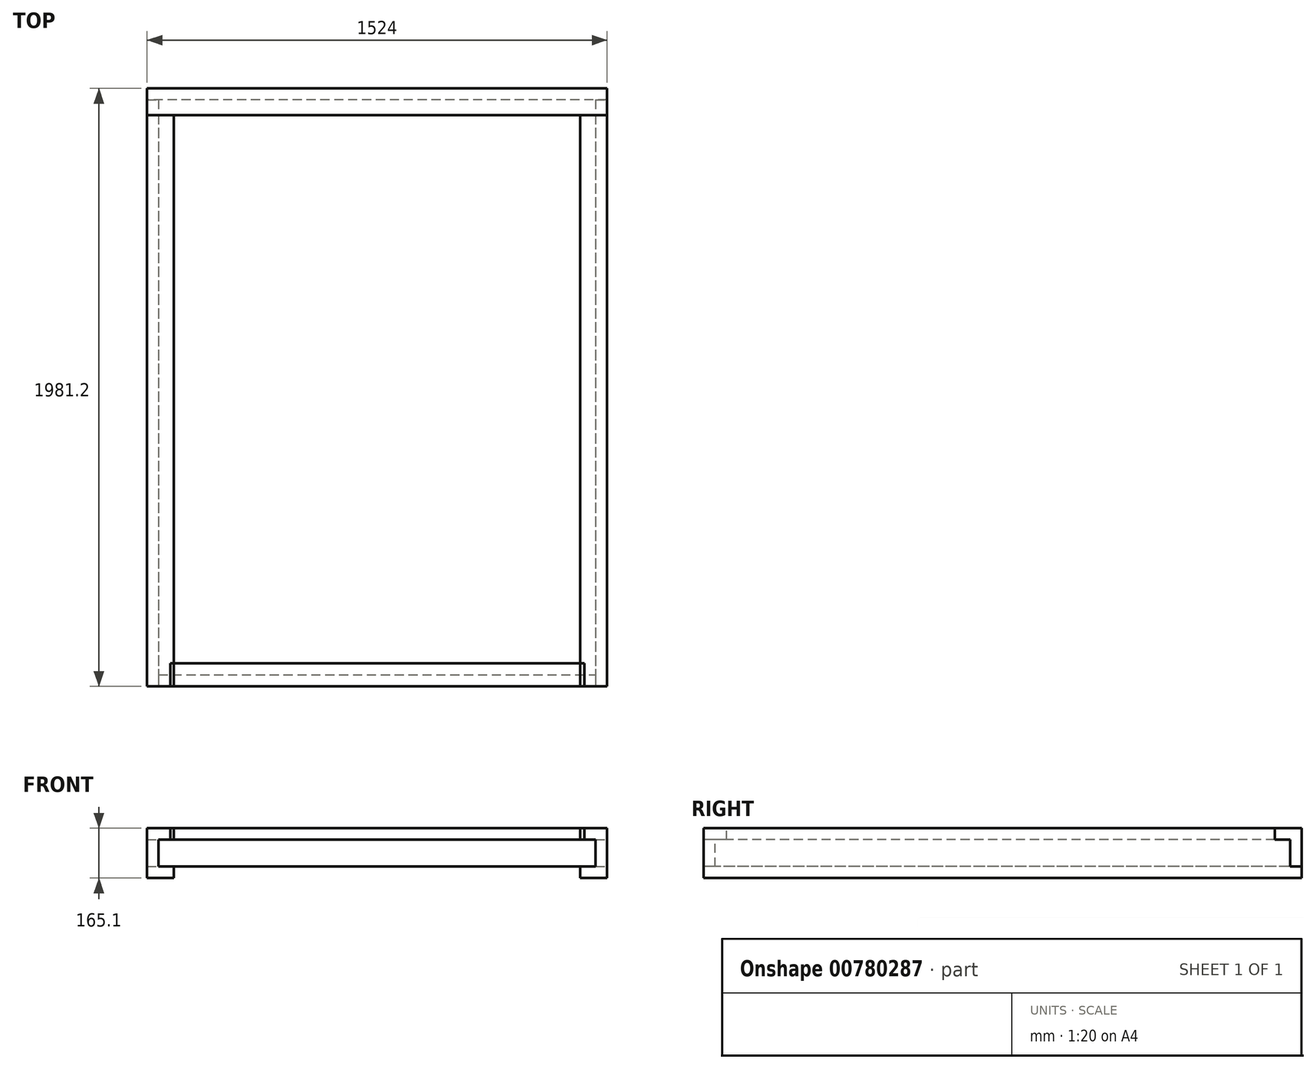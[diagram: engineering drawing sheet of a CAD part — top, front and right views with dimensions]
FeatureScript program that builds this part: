
annotation { "Feature Type Name" : "Feature", "Feature Type Description" : "" }
export const myFeature = defineFeature(function(context is Context, id is Id, definition is map)
    precondition{}
    {
        {
            var Q0;
            Q0=qCreatedBy(makeId("Front.planeOp"),FACE);
            var sketch = newSketch(context, id + "F0", { "sketchPlane" : qUnion([Q0])});
            skLineSegment(sketch, "E0", {"start": v(0, 0) * mm, "end": v(88.9, 0) * mm});
            skLineSegment(sketch, "E1", {"start": v(88.9, 0) * mm, "end": v(88.9, 38.1) * mm});
            skLineSegment(sketch, "E2", {"start": v(88.9, 38.1) * mm, "end": v(0, 38.1) * mm});
            skLineSegment(sketch, "E3", {"start": v(0, 38.1) * mm, "end": v(0, 0) * mm});
            skLineSegment(sketch, "E4.bottom", {"start": v(0, 38.1) * mm, "end": v(38.1, 38.1) * mm});
            skLineSegment(sketch, "E4.top", {"start": v(0, 127) * mm, "end": v(38.1, 127) * mm});
            skLineSegment(sketch, "E4.left", {"start": v(0, 38.1) * mm, "end": v(0, 127) * mm});
            skLineSegment(sketch, "E4.right", {"start": v(38.1, 38.1) * mm, "end": v(38.1, 127) * mm});
            skLineSegment(sketch, "E5.bottom", {"start": v(0, 127) * mm, "end": v(88.9, 127) * mm});
            skLineSegment(sketch, "E5.top", {"start": v(0, 165.1) * mm, "end": v(88.9, 165.1) * mm});
            skLineSegment(sketch, "E5.left", {"start": v(0, 127) * mm, "end": v(0, 165.1) * mm});
            skLineSegment(sketch, "E5.right", {"start": v(88.9, 127) * mm, "end": v(88.9, 165.1) * mm});
            skSolve(sketch);
        }
        {
            var Q0;
            Q0 = qSketchRegion(id + "F0", true);
            extrude(context, id + "F1", {"entities" : qUnion([Q0]), "oppositeDirection" : true, "depth" : 1981.2 * mm, "offsetDistance" : 25.4 * mm});
        }
        {
            var Q0;
            Q0=qCreatedBy(makeId("Right.planeOp"),FACE);
            cPlane(context, id + "F2", {"entities" : qUnion([Q0]), "cplaneType" : CPlaneType.OFFSET, "offset" : 762 * mm, "width" : 152.4 * mm, "height" : 152.4 * mm});
        }
        {
            var Q0;
            Q0=makeQuery(id+"F1.opExtrude","SWEPT_BODY",BODY,{"disambiguationData":[OSD([sQuery(id+"F0.wireOp",EDGE,"E0"),sQuery(id+"F0.wireOp",EDGE,"E1"),sQuery(id+"F0.wireOp",EDGE,"E2"),sQuery(id+"F0.wireOp",EDGE,"E3"),sQuery(id+"F0.wireOp",EDGE,"E4.left"),sQuery(id+"F0.wireOp",EDGE,"E4.right"),sQuery(id+"F0.wireOp",EDGE,"E5.bottom"),sQuery(id+"F0.wireOp",EDGE,"E5.top"),sQuery(id+"F0.wireOp",EDGE,"E5.left"),sQuery(id+"F0.wireOp",EDGE,"E5.right")])]});
            var Q1;
            Q1=qCreatedBy(id+"F2.planeOp",FACE);
            mirror(context, id + "F3", {"entities" : qUnion([Q0]), "mirrorPlane" : qUnion([Q1])});
        }
        {
            var Q0;
            Q0=makeQuery(id+"F1.opExtrude","SWEPT_FACE",FACE,{"disambiguationData":[OSD([sQuery(id+"F0.wireOp",EDGE,"E5.top")])]});
            var sketch = newSketch(context, id + "F4", { "sketchPlane" : qUnion([Q0])});
            skLineSegment(sketch, "E6.bottom", {"start": v(0, 1981.2) * mm, "end": v(1524, 1981.2) * mm});
            skLineSegment(sketch, "E6.top", {"start": v(0, 1892.3) * mm, "end": v(1524, 1892.3) * mm});
            skLineSegment(sketch, "E6.left", {"start": v(0, 1981.2) * mm, "end": v(0, 1892.3) * mm});
            skLineSegment(sketch, "E6.right", {"start": v(1524, 1981.2) * mm, "end": v(1524, 1892.3) * mm});
            skSolve(sketch);
        }
        {
            var Q0;
            Q0 = qSketchRegion(id + "F4", true);
            extrude(context, id + "F5", {"entities" : qUnion([Q0]), "operationType" : NewBodyOperationType.REMOVE, "oppositeDirection" : true, "depth" : 38.1 * mm, "offsetDistance" : 25.4 * mm});
        }
        {
            var Q0;
            {var subQ0=sQuery(id+"F0.wireOp",EDGE,"E4.right");var subQ5=sQuery(id+"F4.wireOp",EDGE,"E6.top");Q0=makeQuery(id+"F5.boolean.opBoolean","COPY",FACE,{"disambiguationData":[TD([makeQuery(id+"F1.opExtrude","SWEPT_FACE",FACE,{"disambiguationData":[OSD([subQ0])]})])],"derivedFrom":makeQuery(id+"F5.opExtrude","CAP_FACE",FACE,{"disambiguationData":[OSD([sQuery(id+"F4.wireOp",EDGE,"E6.bottom"),subQ5,sQuery(id+"F4.wireOp",EDGE,"E6.left"),sQuery(id+"F4.wireOp",EDGE,"E6.right")])],"isStart":false})});}
            var sketch = newSketch(context, id + "F6", { "sketchPlane" : qUnion([Q0])});
            skLineSegment(sketch, "E7.bottom", {"start": v(0, 1981.2) * mm, "end": v(1524, 1981.2) * mm});
            skLineSegment(sketch, "E7.top", {"start": v(0, 1943.1) * mm, "end": v(1524, 1943.1) * mm});
            skLineSegment(sketch, "E7.left", {"start": v(0, 1981.2) * mm, "end": v(0, 1943.1) * mm});
            skLineSegment(sketch, "E7.right", {"start": v(1524, 1981.2) * mm, "end": v(1524, 1943.1) * mm});
            skSolve(sketch);
        }
        {
            var Q0;
            {var subQ4=sQuery(id+"F6.wireOp",EDGE,"E7.right");Q0=makeQuery(id+"F6.imprint","IMPRINT",FACE,{"disambiguationData":[TD([[makeQuery(id+"F6.imprint","IMPRINT",EDGE,{"derivedFrom":subQ4}),-1.0]])]});}
            var Q1;
            {var subQ0=sQuery(id+"F6.wireOp",EDGE,"E7.left");Q1=makeQuery(id+"F6.imprint","IMPRINT",FACE,{"disambiguationData":[TD([[makeQuery(id+"F6.imprint","IMPRINT",EDGE,{"derivedFrom":subQ0}),1.0]])]});}
            extrude(context, id + "F7", {"entities" : qUnion([Q0, Q1]), "operationType" : NewBodyOperationType.REMOVE, "oppositeDirection" : true, "depth" : 88.9 * mm, "offsetDistance" : 25.4 * mm});
        }
        {
            var Q0;
            Q0=makeQuery(id+"F1.opExtrude","SWEPT_FACE",FACE,{"disambiguationData":[OSD([sQuery(id+"F0.wireOp",EDGE,"E3"),sQuery(id+"F0.wireOp",EDGE,"E4.left"),sQuery(id+"F0.wireOp",EDGE,"E5.left")])]});
            var sketch = newSketch(context, id + "F8", { "sketchPlane" : qUnion([Q0])});
            skLineSegment(sketch, "E8", {"start": v(-1892.3, 165.1) * mm, "end": v(-1981.2, 165.1) * mm});
            skLineSegment(sketch, "E9", {"start": v(-1981.2, 165.1) * mm, "end": v(-1981.2, 38.1) * mm});
            skLineSegment(sketch, "E10", {"start": v(-1981.2, 38.1) * mm, "end": v(-1943.1, 38.1) * mm});
            skLineSegment(sketch, "E11", {"start": v(-1943.1, 38.1) * mm, "end": v(-1943.1, 127) * mm});
            skLineSegment(sketch, "E12", {"start": v(-1943.1, 127) * mm, "end": v(-1892.3, 127) * mm});
            skLineSegment(sketch, "E13", {"start": v(-1892.3, 127) * mm, "end": v(-1892.3, 165.1) * mm});
            skSolve(sketch);
        }
        {
            var Q0;
            Q0 = qSketchRegion(id + "F8", true);
            extrude(context, id + "F9", {"entities" : qUnion([Q0]), "oppositeDirection" : true, "depth" : 1524 * mm, "offsetDistance" : 25.4 * mm});
        }
        {
            var Q0;
            Q0=makeQuery(id+"F1.opExtrude","CAP_FACE",FACE,{"disambiguationData":[OSD([sQuery(id+"F0.wireOp",EDGE,"E0"),sQuery(id+"F0.wireOp",EDGE,"E1"),sQuery(id+"F0.wireOp",EDGE,"E2"),sQuery(id+"F0.wireOp",EDGE,"E3"),sQuery(id+"F0.wireOp",EDGE,"E4.left"),sQuery(id+"F0.wireOp",EDGE,"E4.right"),sQuery(id+"F0.wireOp",EDGE,"E5.bottom"),sQuery(id+"F0.wireOp",EDGE,"E5.top"),sQuery(id+"F0.wireOp",EDGE,"E5.left"),sQuery(id+"F0.wireOp",EDGE,"E5.right")])],"isStart":true});
            var sketch = newSketch(context, id + "F10", { "sketchPlane" : qUnion([Q0])});
            skLineSegment(sketch, "E14.bottom", {"start": v(38.1, 127) * mm, "end": v(1485.9, 127) * mm});
            skLineSegment(sketch, "E14.top", {"start": v(38.1, 38.1) * mm, "end": v(1485.9, 38.1) * mm});
            skLineSegment(sketch, "E14.left", {"start": v(38.1, 127) * mm, "end": v(38.1, 38.1) * mm});
            skLineSegment(sketch, "E14.right", {"start": v(1485.9, 127) * mm, "end": v(1485.9, 38.1) * mm});
            skSolve(sketch);
        }
        {
            var Q0;
            Q0 = qSketchRegion(id + "F10", true);
            extrude(context, id + "F11", {"entities" : qUnion([Q0]), "oppositeDirection" : true, "depth" : 38.1 * mm, "offsetDistance" : 25.4 * mm});
        }
        {
            var Q0;
            Q0=makeQuery(id+"F11.opExtrude","CAP_FACE",FACE,{"disambiguationData":[OSD([sQuery(id+"F10.wireOp",EDGE,"E14.bottom"),sQuery(id+"F10.wireOp",EDGE,"E14.top"),sQuery(id+"F10.wireOp",EDGE,"E14.left"),sQuery(id+"F10.wireOp",EDGE,"E14.right")])],"isStart":true});
            var sketch = newSketch(context, id + "F12", { "sketchPlane" : qUnion([Q0])});
            skLineSegment(sketch, "E15.bottom", {"start": v(76.36, 127) * mm, "end": v(1447.96, 127) * mm});
            skLineSegment(sketch, "E15.top", {"start": v(76.36, 165.1) * mm, "end": v(1447.96, 165.1) * mm});
            skLineSegment(sketch, "E15.left", {"start": v(76.36, 127) * mm, "end": v(76.36, 165.1) * mm});
            skLineSegment(sketch, "E15.right", {"start": v(1447.96, 127) * mm, "end": v(1447.96, 165.1) * mm});
            skSolve(sketch);
        }
        {
            var Q0;
            Q0 = qSketchRegion(id + "F12", true);
            extrude(context, id + "F13", {"entities" : qUnion([Q0]), "oppositeDirection" : true, "depth" : 76.2 * mm, "offsetDistance" : 25.4 * mm});
        }
    });
